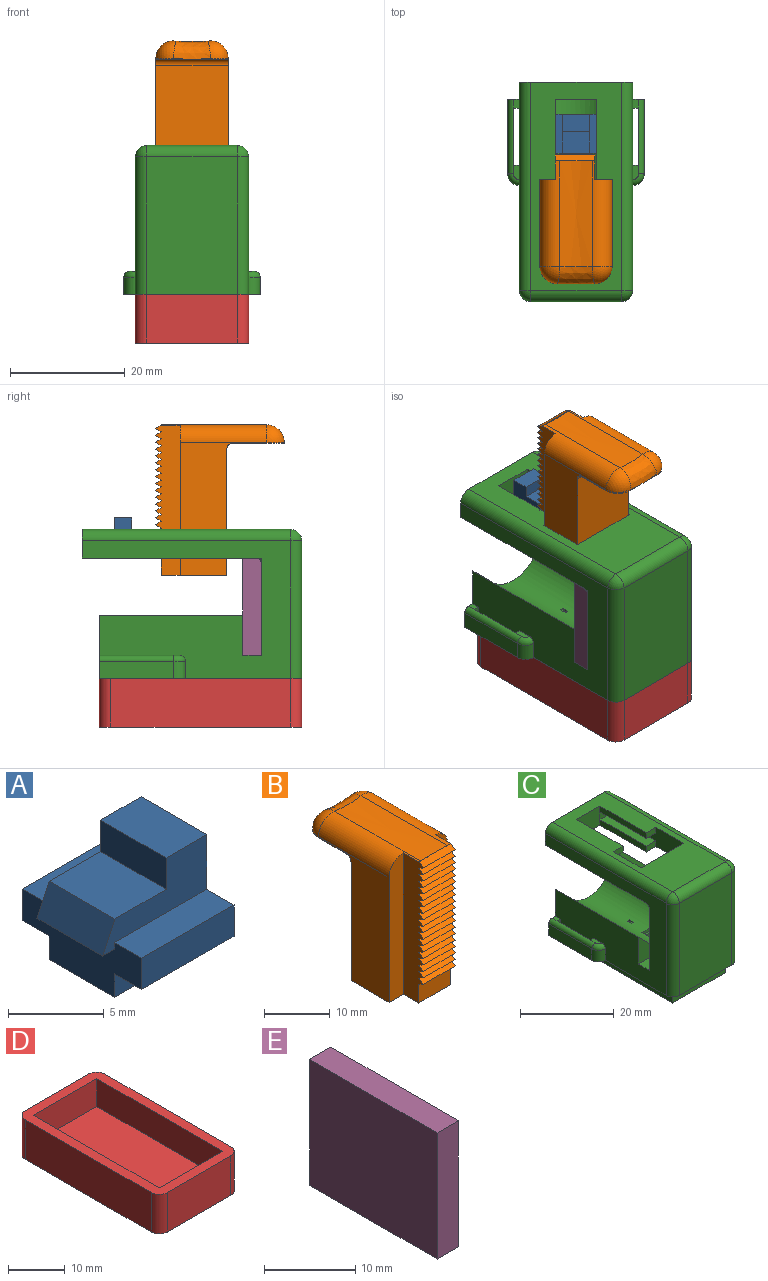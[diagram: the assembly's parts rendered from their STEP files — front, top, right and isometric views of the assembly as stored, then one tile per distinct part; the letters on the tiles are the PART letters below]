
ASSEMBLY  parts=5 mates=4
PART A: 18 faces, bbox 7.7x8.8x7 mm
  f0: plane 7.7x3.92mm, normal (0,1,0), area 17.1mm2, adj f3,f5,f6,f8,f9,f13,f16,f17
  f1: plane 6.8x1.5mm, normal (0,-1,0), area 10.2mm2, adj f3,f5,f7,f11
  f2: plane 6.8x1.5mm, normal (0,1,0), area 10.2mm2, adj f3,f5,f7,f14
  f3: plane 8.84x3.5mm, normal (-1,0,0), area 22.9mm2, adj f0,f1,f2,f4,f7,f10,f11,f12
  f4: plane 7.7x3.92mm, normal (0,-1,0), area 17.1mm2, adj f3,f5,f6,f8,f9,f10,f16,f17
  f5: plane 8.84x7mm, normal (1,0,0), area 41.9mm2, adj f0,f1,f2,f4,f7,f9,f10,f11
  f6: plane 4.84x3.8mm, normal (0,0,1), area 18.4mm2, adj f0,f4,f8,f16
  f7: plane 6.8x4.84mm, normal (0,0,-1), area 32.9mm2, adj f1,f2,f3,f5
  f8: plane 4.84x2mm, normal (-1,0,0), area 9.7mm2, adj f0,f4,f6,f9
  f9: plane 4.84x3mm, normal (0,0,1), area 14.5mm2, adj f0,f4,f5,f8
  f10: plane 6.8x2mm, normal (0,0,1), area 13.6mm2, adj f3,f4,f5,f12
  f11: plane 6.8x2mm, normal (0,0,-1), area 13.6mm2, adj f1,f3,f5,f12
  f12: plane 6.8x2mm, normal (0,-1,0), area 13.6mm2, adj f3,f5,f10,f11
  f13: plane 6.8x2mm, normal (0,0,1), area 13.6mm2, adj f0,f3,f5,f15
  f14: plane 6.8x2mm, normal (0,0,-1), area 13.6mm2, adj f2,f3,f5,f15
  f15: plane 6.8x2mm, normal (0,1,0), area 13.6mm2, adj f3,f5,f13,f14
  f16: plane 4.84x1.92mm, normal (-0.91,0,0.42), area 10.3mm2, adj f0,f4,f6,f17
  f17: plane 4.84x0.9mm, normal (0,0,-1), area 4.3mm2, adj f0,f3,f4,f16
PART B: 62 faces, bbox 12.6x22.5x26.7 mm
  f0: plane 0.22x0.01mm, normal (0,-1,0), area 0mm2, adj f6,f19,f24
  f1: plane 0.58x0.01mm, normal (0,-1,0), area 0mm2, adj f20,f24
  f2: plane 2.33x0.23mm, normal (0,1,0), area 0.2mm2, adj f12,f16,f17
  f3: plane 22x12.6mm, normal (0,1,0), area 277.2mm2, adj f4,f10,f11,f14
  f4: plane 23.22x15.15mm, normal (-1,0,0), area 191mm2, adj f3,f5,f11,f12,f14,f17,f19
  f5: plane 26.22x3.07mm, normal (0,-1,0), area 78.6mm2, adj f4,f6,f11,f19
  f6: plane 26.22x4.34mm, normal (-1,0,0), area 98.5mm2, adj f0,f5,f7,f11,f19,f24,f25,f26
  f7: plane 6.82x3.41mm, normal (0,-1,0), area 23.2mm2, adj f6,f8,f11,f61
  f8: plane 26.21x4.34mm, normal (1,0,0), area 98.4mm2, adj f7,f9,f11,f20,f24,f25,f26,f27
  f9: plane 26.21x2.71mm, normal (0,-1,0), area 69.1mm2, adj f8,f10,f11,f20
  f10: plane 23.22x15.15mm, normal (1,0,0), area 191mm2, adj f3,f9,f11,f12,f14,f20,f22
  f11: plane 12.6x11.45mm, normal (0,0,-1), area 125.2mm2, adj f3,f4,f5,f6,f7,f8,f9,f10
  f12: plane 12.64x9.04mm, normal (0,0,-1), area 109.5mm2, adj f2,f4,f10,f13,f14,f16,f17,f22
  f13: plane 2.33x0.23mm, normal (0,1,0), area 0.2mm2, adj f12,f16,f22
  f14: cylinder r=1mm len=12.6mm, axis (-1,0,0), area 19.8mm2, adj f3,f4,f10,f12
  f15: extruded ~18.45x5.73mm, area 106mm2, adj f16,f19,f20,f23
  f16: bspline ~10.13x3.7mm, area 28.6mm2, adj f2,f12,f13,f15,f18,f21
  f17: cylinder r=3mm len=3mm, axis (0,0,-1), area 1mm2, adj f2,f4,f12,f18
  f18: sphere r=3mm, area 10mm2, adj f16,f17,f19
  f19: cylinder r=3mm len=18.45mm, axis (0,1,0), area 79.3mm2, adj f0,f4,f5,f6,f15,f18,f23
  f20: cylinder r=3mm len=18.45mm, axis (0,1,0), area 80.4mm2, adj f1,f8,f9,f10,f15,f21,f23
  f21: sphere r=3mm, area 26.3mm2, adj f16,f20,f22
  f22: cylinder r=3mm len=3mm, axis (0,0,-1), area 1mm2, adj f10,f12,f13,f21
  f23: plane 6.02x0.37mm, normal (0,1,0), area 0.9mm2, adj f15,f19,f20,f24
  f24: plane 6.82x1.04mm, normal (0,-0.5,0.87), area 8.2mm2, adj f0,f1,f6,f8,f23,f25
  f25: plane 6.82x1.04mm, normal (0,-0.5,-0.87), area 8.2mm2, adj f6,f8,f24,f26
  f26: plane 6.82x1.04mm, normal (0,-0.5,0.87), area 8.2mm2, adj f6,f8,f25,f27
  f27: plane 6.82x1.04mm, normal (0,-0.5,-0.87), area 8.2mm2, adj f6,f8,f26,f28
  f28: plane 6.82x1.04mm, normal (0,-0.5,0.87), area 8.2mm2, adj f6,f8,f27,f29
  f29: plane 6.82x1.04mm, normal (0,-0.5,-0.87), area 8.2mm2, adj f6,f8,f28,f30
  f30: plane 6.82x1.04mm, normal (0,-0.5,0.87), area 8.2mm2, adj f6,f8,f29,f31
  f31: plane 6.82x1.04mm, normal (0,-0.5,-0.87), area 8.2mm2, adj f6,f8,f30,f32
  f32: plane 6.82x1.04mm, normal (0,-0.5,0.87), area 8.2mm2, adj f6,f8,f31,f33
  f33: plane 6.82x1.04mm, normal (0,-0.5,-0.87), area 8.2mm2, adj f6,f8,f32,f34
  f34: plane 6.82x1.04mm, normal (0,-0.5,0.87), area 8.2mm2, adj f6,f8,f33,f35
  f35: plane 6.82x1.04mm, normal (0,-0.5,-0.87), area 8.2mm2, adj f6,f8,f34,f36
  f36: plane 6.82x1.04mm, normal (0,-0.5,0.87), area 8.2mm2, adj f6,f8,f35,f37
  f37: plane 6.82x1.04mm, normal (0,-0.5,-0.87), area 8.2mm2, adj f6,f8,f36,f38
  f38: plane 6.82x1.04mm, normal (0,-0.5,0.87), area 8.2mm2, adj f6,f8,f37,f39
  f39: plane 6.82x1.04mm, normal (0,-0.5,-0.87), area 8.2mm2, adj f6,f8,f38,f40
  f40: plane 6.82x1.04mm, normal (0,-0.5,0.87), area 8.2mm2, adj f6,f8,f39,f41
  f41: plane 6.82x1.04mm, normal (0,-0.5,-0.87), area 8.2mm2, adj f6,f8,f40,f42
  f42: plane 6.82x1.04mm, normal (0,-0.5,0.87), area 8.2mm2, adj f6,f8,f41,f43
  f43: plane 6.82x1.04mm, normal (0,-0.5,-0.87), area 8.2mm2, adj f6,f8,f42,f44
  f44: plane 6.82x1.04mm, normal (0,-0.5,0.87), area 8.2mm2, adj f6,f8,f43,f45
  f45: plane 6.82x1.04mm, normal (0,-0.5,-0.87), area 8.2mm2, adj f6,f8,f44,f46
  f46: plane 6.82x1.04mm, normal (0,-0.5,0.87), area 8.2mm2, adj f6,f8,f45,f47
  f47: plane 6.82x1.04mm, normal (0,-0.5,-0.87), area 8.2mm2, adj f6,f8,f46,f48
  f48: plane 6.82x1.04mm, normal (0,-0.5,0.87), area 8.2mm2, adj f6,f8,f47,f49
  f49: plane 6.82x1.04mm, normal (0,-0.5,-0.87), area 8.2mm2, adj f6,f8,f48,f50
  f50: plane 6.82x1.04mm, normal (0,-0.5,0.87), area 8.2mm2, adj f6,f8,f49,f51
  f51: plane 6.82x1.04mm, normal (0,-0.5,-0.87), area 8.2mm2, adj f6,f8,f50,f52
  f52: plane 6.82x1.04mm, normal (0,-0.5,0.87), area 8.2mm2, adj f6,f8,f51,f53
  f53: plane 6.82x1.04mm, normal (0,-0.5,-0.87), area 8.2mm2, adj f6,f8,f52,f54
  f54: plane 6.82x1.04mm, normal (0,-0.5,0.87), area 8.2mm2, adj f6,f8,f53,f55
  f55: plane 6.82x1.04mm, normal (0,-0.5,-0.87), area 8.2mm2, adj f6,f8,f54,f56
  f56: plane 6.82x1.04mm, normal (0,-0.5,0.87), area 8.2mm2, adj f6,f8,f55,f57
  f57: plane 6.82x1.04mm, normal (0,-0.5,-0.87), area 8.2mm2, adj f6,f8,f56,f58
  f58: plane 6.82x1.04mm, normal (0,-0.5,0.87), area 8.2mm2, adj f6,f8,f57,f59
  f59: plane 6.82x1.04mm, normal (0,-0.5,-0.87), area 8.2mm2, adj f6,f8,f58,f60
  f60: plane 6.82x1.04mm, normal (0,-0.5,0.87), area 8.2mm2, adj f6,f8,f59,f61
  f61: plane 6.82x1.04mm, normal (0,-0.5,-0.87), area 8.2mm2, adj f6,f7,f8,f60
PART C: 88 faces, bbox 24.1x38.3x29 mm
  f0: plane 2.89x1.5mm, normal (0,-1,0), area 4.3mm2, adj f4,f60,f64,f85
  f1: plane 13.97x1.5mm, normal (1,0,0), area 20.9mm2, adj f7,f8,f81,f86
  f2: plane 2.89x1.5mm, normal (0,-1,0), area 4.3mm2, adj f4,f62,f63,f82
  f3: plane 13.97x1.5mm, normal (-1,0,0), area 20.9mm2, adj f8,f59,f81,f83
  f4: plane 36.3x15.78mm, normal (0,0,1), area 368.5mm2, adj f0,f2,f42,f60,f61,f62,f63,f64
  f5: plane 24x11.78mm, normal (0,0,-1), area 276.8mm2, adj f15,f16,f17,f18,f33,f34,f35,f36
  f6: cylinder r=7mm len=25mm, axis (0,1,0), area 262.3mm2, adj f13,f19,f21,f22,f23,f25,f26,f27
  f7: plane 2.89x1.5mm, normal (0,-1,0), area 4.3mm2, adj f1,f8,f60,f86
  f8: plane 30.3x19.78mm, normal (0,0,-1), area 395.1mm2, adj f1,f3,f7,f12,f20,f41,f59,f60
  f9: plane 2.5x1mm, normal (0,0,1), area 2.3mm2, adj f12,f48,f49,f58
  f10: plane 35.3x23.78mm, normal (0,0,-1), area 240.9mm2, adj f12,f19,f20,f30,f31,f32,f37,f38
  f11: plane 2.5x1mm, normal (0,0,1), area 2.3mm2, adj f20,f51,f52,f54
  f12: plane 36.3x24mm, normal (-1,0,0), area 482.6mm2, adj f8,f9,f10,f13,f19,f22,f24,f40
  f13: plane 9.57x6.99mm, normal (0,-1,0), area 25.5mm2, adj f6,f12,f22,f40
  f14: plane 31.3x15.78mm, normal (0,0,-1), area 211.2mm2, adj f30,f31,f32,f33,f34,f35,f36,f38
  f15: plane 1.5x1.5mm, normal (0,1,0), area 2.2mm2, adj f5,f16,f18,f29
  f16: plane 3.7x1.5mm, normal (1,0,0), area 5.5mm2, adj f5,f15,f17,f29
  f17: plane 1.5x1.5mm, normal (0,-1,0), area 2.2mm2, adj f5,f16,f18,f29
  f18: plane 3.7x1.5mm, normal (-1,0,0), area 5.5mm2, adj f5,f15,f17,f29
  f19: plane 23.78x11mm, normal (0,1,0), area 145.8mm2, adj f6,f10,f12,f20,f21,f22,f43,f44
  f20: plane 36.3x24mm, normal (1,0,0), area 482.6mm2, adj f8,f10,f11,f19,f21,f23,f24,f40
  f21: plane 25x4.72mm, normal (-0.71,0,0.71), area 167mm2, adj f6,f19,f20,f23
  f22: plane 25x5.17mm, normal (0.71,0,0.71), area 182.7mm2, adj f6,f12,f13,f19
  f23: plane 9.57x6.99mm, normal (0,-1,0), area 25.5mm2, adj f6,f20,f21,f40
  f24: plane 19.78x15.99mm, normal (0,1,0), area 316.3mm2, adj f12,f20,f40,f41
  f25: plane 4.7x0.87mm, normal (-1,0,0), area 4.1mm2, adj f6,f26,f28,f29
  f26: plane 2.5x0.87mm, normal (0,1,0), area 2mm2, adj f6,f25,f27,f29
  f27: plane 4.7x0.87mm, normal (1,0,0), area 4.1mm2, adj f6,f26,f28,f29
  f28: plane 2.5x0.87mm, normal (0,-1,0), area 2mm2, adj f6,f25,f27,f29
  f29: plane 4.7x2.5mm, normal (0,0,1), area 6.2mm2, adj f15,f16,f17,f18,f25,f26,f27,f28
  f30: plane 31.3x3mm, normal (-1,0,0), area 93.9mm2, adj f10,f14,f32,f38
  f31: plane 31.3x3mm, normal (1,0,0), area 93.9mm2, adj f10,f14,f32,f38
  f32: plane 15.78x3mm, normal (0,1,0), area 47.3mm2, adj f10,f14,f30,f31
  f33: plane 11.78x4.74mm, normal (0,1,0), area 55.8mm2, adj f5,f14,f34,f36
  f34: plane 24x4.74mm, normal (1,0,0), area 113.8mm2, adj f5,f14,f33,f35
  f35: plane 11.78x4.74mm, normal (0,-1,0), area 55.8mm2, adj f5,f14,f34,f36
  f36: plane 24x4.74mm, normal (-1,0,0), area 113.8mm2, adj f5,f14,f33,f35
  f37: plane 24x15.78mm, normal (0,-1,0), area 378.7mm2, adj f10,f42,f74,f77
  f38: plane 15.78x3mm, normal (0,-1,0), area 47.3mm2, adj f10,f14,f30,f31
  f39: plane 0.64x0.01mm, normal (0,1,0), area 0mm2, adj f6,f40
  f40: plane 19.78x3.3mm, normal (0,0,1), area 65.3mm2, adj f12,f13,f20,f23,f24,f39
  f41: cylinder r=1mm len=19.78mm, axis (-1,0,0), area 31.1mm2, adj f8,f12,f20,f24
  f42: cylinder r=2mm len=15.78mm, axis (-1,0,0), area 49.6mm2, adj f4,f37,f75,f78
  f43: plane 1.5x1mm, normal (0,0,1), area 1.5mm2, adj f19,f20,f51,f53
  f44: plane 13x3mm, normal (1,0,0), area 39mm2, adj f10,f19,f50,f51
  f45: plane 1.5x1mm, normal (0,0,1), area 1.5mm2, adj f12,f19,f48,f56
  f46: plane 13x3mm, normal (-1,0,0), area 39mm2, adj f10,f19,f47,f48
  f47: cylinder r=2mm len=3mm, axis (0,0,-1), area 9.4mm2, adj f10,f12,f46,f49
  f48: cylinder r=1mm len=13mm, axis (0,-1,0), area 20.4mm2, adj f9,f19,f45,f46,f49,f57
  f49: torus R=1mm, axis (0,0,1), area 4mm2, adj f9,f12,f47,f48
  f50: cylinder r=2mm len=3mm, axis (0,0,1), area 9.4mm2, adj f10,f20,f44,f52
  f51: cylinder r=1mm len=13mm, axis (0,1,0), area 20.4mm2, adj f11,f19,f43,f44,f52,f55
  f52: torus R=1mm, axis (0,0,-1), area 4mm2, adj f11,f20,f50,f51
  f53: plane 4x1mm, normal (0,-1,0), area 4mm2, adj f10,f20,f43,f55
  f54: plane 4x1mm, normal (0,1,0), area 4mm2, adj f10,f11,f20,f55
  f55: plane 10x4mm, normal (-1,0,0), area 40mm2, adj f10,f51,f53,f54
  f56: plane 4x1mm, normal (0,-1,0), area 4mm2, adj f10,f12,f45,f57
  f57: plane 10x4mm, normal (1,0,0), area 40mm2, adj f10,f48,f56,f58
  f58: plane 4x1mm, normal (0,1,0), area 4mm2, adj f9,f10,f12,f57
  f59: plane 2.89x1.5mm, normal (0,-1,0), area 4.3mm2, adj f3,f8,f62,f83
  f60: plane 22.3x5mm, normal (1,0,0), area 69.6mm2, adj f0,f4,f7,f8,f61,f85,f86,f87
  f61: plane 12.78x5mm, normal (0,1,0), area 63.9mm2, adj f4,f8,f60,f62
  f62: plane 22.3x5mm, normal (-1,0,0), area 69.6mm2, adj f2,f4,f8,f59,f61,f82,f83,f84
  f63: plane 13.97x1.5mm, normal (-1,0,0), area 21mm2, adj f2,f4,f81,f82
  f64: plane 13.97x1.5mm, normal (1,0,0), area 21mm2, adj f0,f4,f81,f85
  f65: plane 1.15x0.32mm, normal (-1,0,0), area 0.4mm2, adj f6,f66,f68,f69
  f66: plane 0.65x0.32mm, normal (0,1,0), area 0.2mm2, adj f6,f65,f67,f69
  f67: plane 1.15x0.32mm, normal (1,0,0), area 0.4mm2, adj f6,f66,f68,f69
  f68: plane 0.65x0.32mm, normal (0,-1,0), area 0.2mm2, adj f6,f65,f67,f69
  f69: plane 1.15x0.65mm, normal (0,0,1), area 0.4mm2, adj f65,f66,f67,f68,f70,f71,f72,f73
  f70: plane 1.95x0.39mm, normal (0,1,0), area 0.8mm2, adj f5,f69,f71,f73
  f71: plane 1.95x0.89mm, normal (-1,0,0), area 1.7mm2, adj f5,f69,f70,f72
  f72: plane 1.95x0.39mm, normal (0,-1,0), area 0.8mm2, adj f5,f69,f71,f73
  f73: plane 1.95x0.89mm, normal (1,0,0), area 1.7mm2, adj f5,f69,f70,f72
  f74: cylinder r=2mm len=24mm, axis (0,0,-1), area 75.4mm2, adj f10,f20,f37,f75
  f75: sphere r=2mm, area 6.3mm2, adj f42,f74,f76
  f76: cylinder r=2mm len=36.3mm, axis (0,-1,0), area 114mm2, adj f4,f20,f75,f80
  f77: cylinder r=2mm len=24mm, axis (0,0,1), area 75.4mm2, adj f10,f12,f37,f78
  f78: sphere r=2mm, area 6.3mm2, adj f42,f77,f79
  f79: cylinder r=2mm len=36.3mm, axis (0,1,0), area 114mm2, adj f4,f12,f78,f80
  f80: plane 19.78x5mm, normal (0,1,0), area 97.2mm2, adj f4,f8,f12,f20,f76,f79
  f81: plane 7x5mm, normal (0,-1,0), area 35mm2, adj f1,f3,f4,f8,f63,f64,f84,f87
  f82: plane 13.97x2.89mm, normal (0,0,-1), area 40.4mm2, adj f2,f62,f63,f84
  f83: plane 13.97x2.89mm, normal (0,0,1), area 40.4mm2, adj f3,f59,f62,f84
  f84: plane 2.89x2mm, normal (0,-1,0), area 5.8mm2, adj f62,f81,f82,f83
  f85: plane 13.97x2.89mm, normal (0,0,-1), area 40.4mm2, adj f0,f60,f64,f87
  f86: plane 13.97x2.89mm, normal (0,0,1), area 40.4mm2, adj f1,f7,f60,f87
  f87: plane 2.89x2mm, normal (0,-1,0), area 5.8mm2, adj f60,f81,f85,f86
PART D: 15 faces, bbox 19.8x35.3x8.5 mm
  f0: plane 35.3x19.78mm, normal (0,0,1), area 200.9mm2, adj f1,f2,f3,f4,f6,f7,f8,f9
  f1: plane 15.78x8.5mm, normal (0,1,0), area 134.1mm2, adj f0,f5,f11,f12
  f2: plane 31.3x8.5mm, normal (-1,0,0), area 266.1mm2, adj f0,f5,f11,f14
  f3: plane 15.78x8.5mm, normal (0,-1,0), area 134.1mm2, adj f0,f5,f13,f14
  f4: plane 31.3x8.5mm, normal (1,0,0), area 266.1mm2, adj f0,f5,f12,f13
  f5: plane 35.3x19.78mm, normal (0,0,-1), area 694.8mm2, adj f1,f2,f3,f4,f11,f12,f13,f14
  f6: plane 15.78x6mm, normal (0,-1,0), area 94.7mm2, adj f0,f7,f9,f10
  f7: plane 31.3x6mm, normal (1,0,0), area 187.8mm2, adj f0,f6,f8,f10
  f8: plane 15.78x6mm, normal (0,1,0), area 94.7mm2, adj f0,f7,f9,f10
  f9: plane 31.3x6mm, normal (-1,0,0), area 187.8mm2, adj f0,f6,f8,f10
  f10: plane 31.3x15.78mm, normal (0,0,1), area 493.9mm2, adj f6,f7,f8,f9
  f11: cylinder r=2mm len=8.5mm, axis (0,0,1), area 26.7mm2, adj f0,f1,f2,f5
  f12: cylinder r=2mm len=8.5mm, axis (0,0,-1), area 26.7mm2, adj f0,f1,f4,f5
  f13: cylinder r=2mm len=8.5mm, axis (0,0,1), area 26.7mm2, adj f0,f3,f4,f5
  f14: cylinder r=2mm len=8.5mm, axis (0,0,-1), area 26.7mm2, adj f0,f2,f3,f5
PART E: 6 faces, bbox 3.3x19.8x16.9 mm
  f0: plane 19.78x3.3mm, normal (0,0,1), area 65.3mm2, adj f1,f3,f4,f5
  f1: plane 19.78x16.9mm, normal (-1,0,0), area 334.3mm2, adj f0,f2,f4,f5
  f2: plane 19.78x3.3mm, normal (0,0,-1), area 65.3mm2, adj f1,f3,f4,f5
  f3: plane 19.78x16.9mm, normal (1,0,0), area 334.3mm2, adj f0,f2,f4,f5
  f4: plane 16.9x3.3mm, normal (0,-1,0), area 55.8mm2, adj f0,f1,f2,f3
  f5: plane 16.9x3.3mm, normal (0,1,0), area 55.8mm2, adj f0,f1,f2,f3
PLACE A rot(axis=(0,0,1),90deg) t=(7.33,10.52,18.52)mm
PLACE B rot(axis=(0,0,-1),180deg) t=(16.59,44.97,15.53)mm
PLACE C rot(axis=(0,-1,0),0deg) t=(3.47,22.7,-5.47)mm
PLACE D rot(axis=(0,-1,0),0deg) t=(12.19,6.89,-10.97)mm fixed
PLACE E rot(axis=(0,0,1),90deg) t=(3.47,-2.09,4.44)mm
MATE fastened D.f12 <-> C.f10  axis (0,0,1) through (21.25,20.7,-2.47)mm
MATE fastened E.f1 <-> C.f24  axis (0,-1,0) through (23.25,-5.6,1.53)mm
MATE slider B.f12 <-> C.f4  axis (0,0,-1) through (13.36,-4.9,38.53)mm
MATE slider A.f5 <-> C.f81  axis (0,1,0) through (13.36,20.05,21.83)mm
